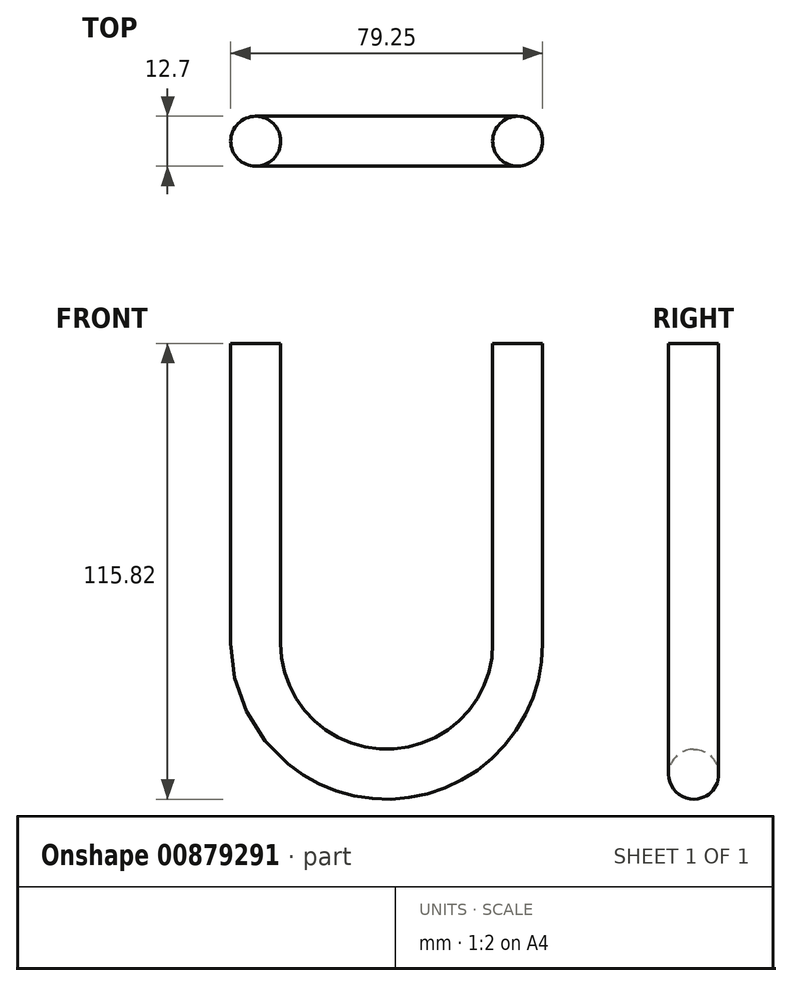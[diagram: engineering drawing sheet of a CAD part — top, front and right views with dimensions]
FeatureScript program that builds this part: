
annotation { "Feature Type Name" : "Feature", "Feature Type Description" : "" }
export const myFeature = defineFeature(function(context is Context, id is Id, definition is map)
    precondition{}
    {
        {
            var Q0;
            Q0=qCreatedBy(makeId("Front.planeOp"),FACE);
            var sketch = newSketch(context, id + "F0", { "sketchPlane" : qUnion([Q0])});
            skLineSegment(sketch, "E0", {"start": v(0, 0) * mm, "end": v(0, 76.2) * mm});
            skLineSegment(sketch, "E1", {"start": v(53.85, 0) * mm, "end": v(53.85, 76.2) * mm});
            skArc(sketch, "E2", {"start": v(0, 0) * mm, "mid": v(26.92, -26.92) * mm, "end": v(53.85, 0) * mm});
            skSolve(sketch);
        }
        {
            var Q0;
            Q0=qCreatedBy(makeId("Top.planeOp"),FACE);
            var Q1;
            Q1=sQuery(id+"F0.wireOp",VERTEX,"E0.end");
            cPlane(context, id + "F1", {"entities" : qUnion([Q0, Q1]), "cplaneType" : CPlaneType.PLANE_POINT, "offset" : 25.4 * mm, "width" : 152.4 * mm, "height" : 152.4 * mm});
        }
        {
            var Q0;
            Q0=qCreatedBy(id+"F1.planeOp",FACE);
            var sketch = newSketch(context, id + "F2", { "sketchPlane" : qUnion([Q0])});
            skCircle(sketch, "E3", {"center": v(-6.35, 0) * mm, "radius": 6.35 * mm});
            skSolve(sketch);
        }
        {
            var Q0;
            Q0=makeQuery(id+"F2.imprint","IMPRINT",FACE,{"disambiguationData":[TD([[makeQuery(id+"F2.imprint","IMPRINT",EDGE,{"derivedFrom":sQuery(id+"F2.wireOp",EDGE,"E3")}),1.0]])]});
            var Q1;
            Q1=sQuery(id+"F0.wireOp",EDGE,"E0");
            var Q2;
            Q2=sQuery(id+"F0.wireOp",EDGE,"E2");
            var Q3;
            Q3=sQuery(id+"F0.wireOp",EDGE,"E1");
            sweep(context, id + "F3", {"profiles" : qUnion([Q0]), "path" : qUnion([Q1, Q2, Q3])});
        }
    });
